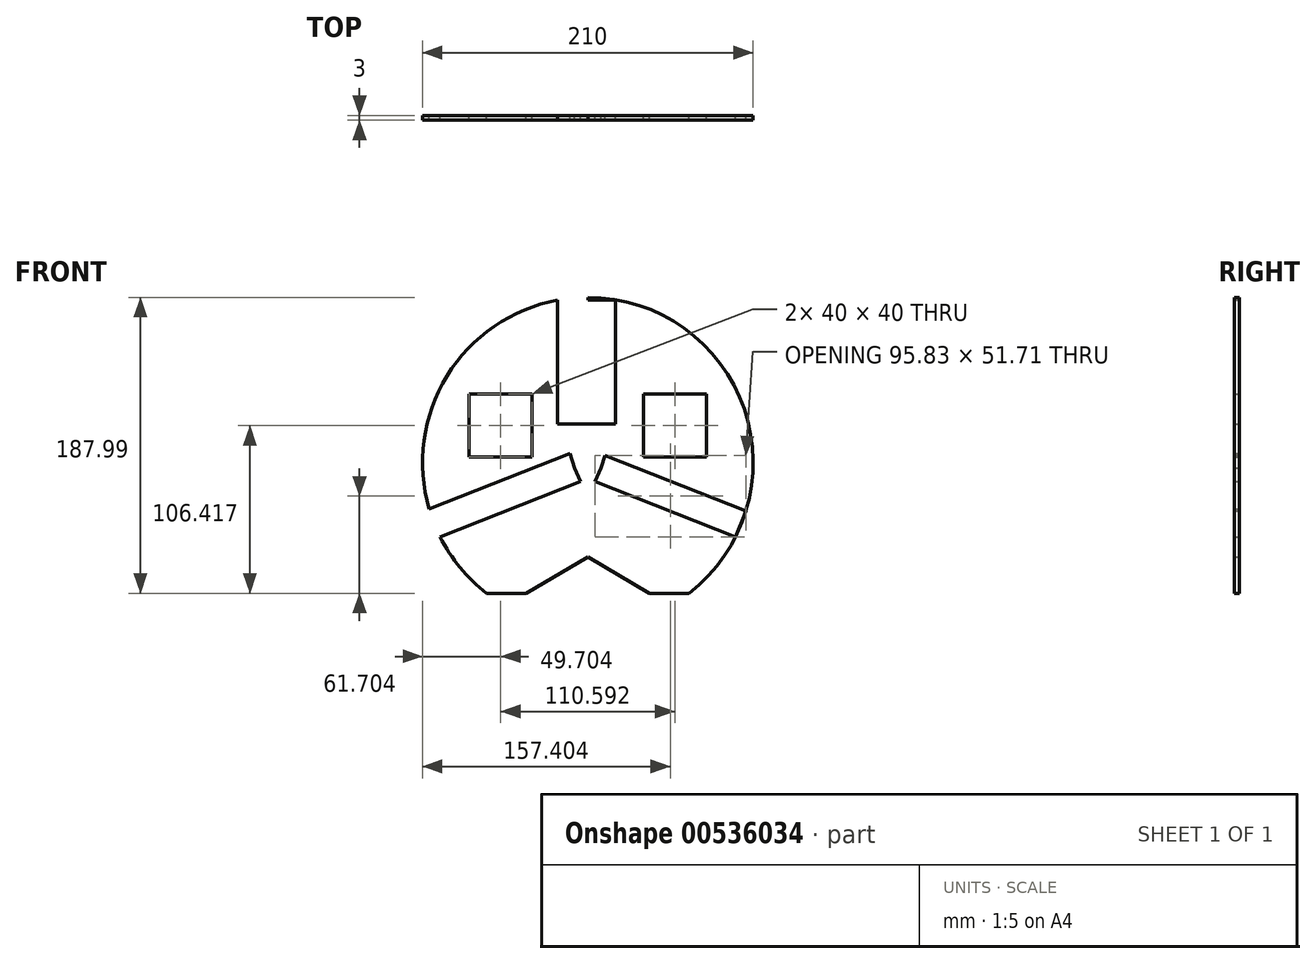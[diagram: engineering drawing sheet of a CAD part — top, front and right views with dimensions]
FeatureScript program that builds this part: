
annotation { "Feature Type Name" : "Feature", "Feature Type Description" : "" }
export const myFeature = defineFeature(function(context is Context, id is Id, definition is map)
    precondition{}
    {
        {
            var Q0;
            Q0=qCreatedBy(makeId("Front.planeOp"),FACE);
            var sketch = newSketch(context, id + "F0", { "sketchPlane" : qUnion([Q0])});
            skCircle(sketch, "E0", {"center": v(0, 0) * mm, "radius": 105 * mm});
            skLineSegment(sketch, "E1", {"start": v(0, 0) * mm, "end": v(0, 105) * mm});
            skLineSegment(sketch, "E2", {"start": v(0, 0) * mm, "end": v(0, -20) * mm});
            skLineSegment(sketch, "E3", {"start": v(0, -20) * mm, "end": v(103.08, -20) * mm});
            skLineSegment(sketch, "E4", {"start": v(0, -20) * mm, "end": v(-103.08, -20) * mm});
            skLineSegment(sketch, "E5", {"start": v(0, -60) * mm, "end": v(-52.62, -90.87) * mm});
            skLineSegment(sketch, "E6", {"start": v(52.62, -90.87) * mm, "end": v(0, -60) * mm});
            skLineSegment(sketch, "E7", {"start": v(-64.32, -83) * mm, "end": v(-39.2, -83) * mm});
            skLineSegment(sketch, "E8", {"start": v(39.2, -83) * mm, "end": v(64.32, -83) * mm});
            skCircle(sketch, "E9.0", {"center": v(0, 0) * mm, "radius": 111.35 * mm});
            skLineSegment(sketch, "E10", {"start": v(-86.17, -60) * mm, "end": v(0, -20) * mm});
            skLineSegment(sketch, "E11", {"start": v(0, -20) * mm, "end": v(86.17, -60) * mm});
            skLineSegment(sketch, "E12.bottom", {"start": v(-19.24, 103.22) * mm, "end": v(17.56, 103.22) * mm});
            skLineSegment(sketch, "E12.top", {"start": v(-19.24, 24.52) * mm, "end": v(17.56, 24.52) * mm});
            skLineSegment(sketch, "E12.left", {"start": v(-19.24, 103.22) * mm, "end": v(-19.24, 24.52) * mm});
            skLineSegment(sketch, "E12.right", {"start": v(17.56, 103.22) * mm, "end": v(17.56, 24.52) * mm});
            skLineSegment(sketch, "E13", {"start": v(97.28, -38.33) * mm, "end": v(100.32, -30.62) * mm});
            skLineSegment(sketch, "E14", {"start": v(-97.3, -38.34) * mm, "end": v(-100.78, -29.52) * mm});
            skLineSegment(sketch, "E15", {"start": v(-97.3, -38.34) * mm, "end": v(-93.85, -47.12) * mm});
            skLineSegment(sketch, "E16", {"start": v(97.28, -38.33) * mm, "end": v(93.8, -47.14) * mm});
            skLineSegment(sketch, "E17", {"start": v(-100.78, -29.52) * mm, "end": v(-93.85, -47.12) * mm});
            skLineSegment(sketch, "E18", {"start": v(100.32, -30.62) * mm, "end": v(93.8, -47.14) * mm});
            skLineSegment(sketch, "E19", {"start": v(-100.78, -29.52) * mm, "end": v(-11.46, 5.67) * mm});
            skLineSegment(sketch, "E20", {"start": v(-11.46, 5.67) * mm, "end": v(-8.37, -3.3) * mm});
            skLineSegment(sketch, "E21", {"start": v(-93.85, -47.12) * mm, "end": v(-4.53, -11.93) * mm});
            skPoint(sketch, "E21.endSnap0", {"position": v(-56.12, -11.93) * mm});
            skLineSegment(sketch, "E22", {"start": v(-8.37, -3.3) * mm, "end": v(-4.53, -11.93) * mm});
            skLineSegment(sketch, "E23", {"start": v(93.8, -47.14) * mm, "end": v(4.5, -11.95) * mm});
            skLineSegment(sketch, "E24", {"start": v(4.5, -11.95) * mm, "end": v(8.37, -3.3) * mm});
            skLineSegment(sketch, "E25", {"start": v(100.32, -30.62) * mm, "end": v(11, 4.57) * mm});
            skLineSegment(sketch, "E26", {"start": v(11, 4.57) * mm, "end": v(8.37, -3.3) * mm});
            skLineSegment(sketch, "E27.bottom", {"start": v(75.3, 3.43) * mm, "end": v(35.3, 3.43) * mm});
            skLineSegment(sketch, "E27.top", {"start": v(75.3, 43.43) * mm, "end": v(35.3, 43.43) * mm});
            skLineSegment(sketch, "E27.left", {"start": v(75.3, 3.43) * mm, "end": v(75.3, 43.43) * mm});
            skLineSegment(sketch, "E27.right", {"start": v(35.3, 3.43) * mm, "end": v(35.3, 43.43) * mm});
            skPoint(sketch, "E27.middle", {"position": v(55.3, 23.43) * mm});
            skPoint(sketch, "E28.middle", {"position": v(-55.3, 23.43) * mm});
            skLineSegment(sketch, "E29.bottom", {"start": v(-75.3, 43.43) * mm, "end": v(-35.3, 43.43) * mm});
            skLineSegment(sketch, "E29.top", {"start": v(-75.3, 3.43) * mm, "end": v(-35.3, 3.43) * mm});
            skLineSegment(sketch, "E29.left", {"start": v(-75.3, 43.43) * mm, "end": v(-75.3, 3.43) * mm});
            skLineSegment(sketch, "E29.right", {"start": v(-35.3, 43.43) * mm, "end": v(-35.3, 3.43) * mm});
            skSolve(sketch);
        }
        {
            var Q0;
            {var subQ13=sQuery(id+"F0.wireOp",EDGE,"E2");Q0=makeQuery(id+"F0.imprint","IMPRINT",FACE,{"disambiguationData":[TD([[makeQuery(id+"F0.imprint","IMPRINT",EDGE,{"derivedFrom":subQ13}),1.0]])]});}
            var Q1;
            {var subQ5=sQuery(id+"F0.wireOp",EDGE,"E2");Q1=makeQuery(id+"F0.imprint","IMPRINT",FACE,{"disambiguationData":[TD([[makeQuery(id+"F0.imprint","IMPRINT",EDGE,{"derivedFrom":subQ5}),-1.0]])]});}
            var Q2;
            {var subQ0=sQuery(id+"F0.wireOp",EDGE,"E4");var subQ1=sQuery(id+"F0.wireOp",EDGE,"E0");var subQ2=makeQuery(id+"F0.imprint","INTERSECT",VERTEX,{"derivedFrom":[subQ1,subQ0]});Q2=makeQuery(id+"F0.imprint","IMPRINT",FACE,{"disambiguationData":[TD([[makeQuery(id+"F0.imprint","IMPRINT",EDGE,{"disambiguationData":[TD([[subQ2,-1.0]])],"derivedFrom":subQ1}),1.0]])]});}
            var Q3;
            {var subQ6=sQuery(id+"F0.wireOp",EDGE,"E11");Q3=makeQuery(id+"F0.imprint","IMPRINT",FACE,{"disambiguationData":[TD([[makeQuery(id+"F0.imprint","IMPRINT",EDGE,{"derivedFrom":subQ6}),1.0]])]});}
            var Q4;
            {var subQ0=sQuery(id+"F0.wireOp",EDGE,"E10");Q4=makeQuery(id+"F0.imprint","IMPRINT",FACE,{"disambiguationData":[TD([[makeQuery(id+"F0.imprint","IMPRINT",EDGE,{"derivedFrom":subQ0}),1.0]])]});}
            var Q5;
            {var subQ3=sQuery(id+"F0.wireOp",EDGE,"E7");Q5=makeQuery(id+"F0.imprint","IMPRINT",FACE,{"disambiguationData":[TD([[makeQuery(id+"F0.imprint","IMPRINT",EDGE,{"derivedFrom":subQ3}),1.0]])]});}
            extrude(context, id + "F1", {"entities" : qUnion([Q0, Q1, Q2, Q3, Q4, Q5]), "depth" : 3 * mm, "offsetDistance" : 25.4 * mm});
        }
    });
